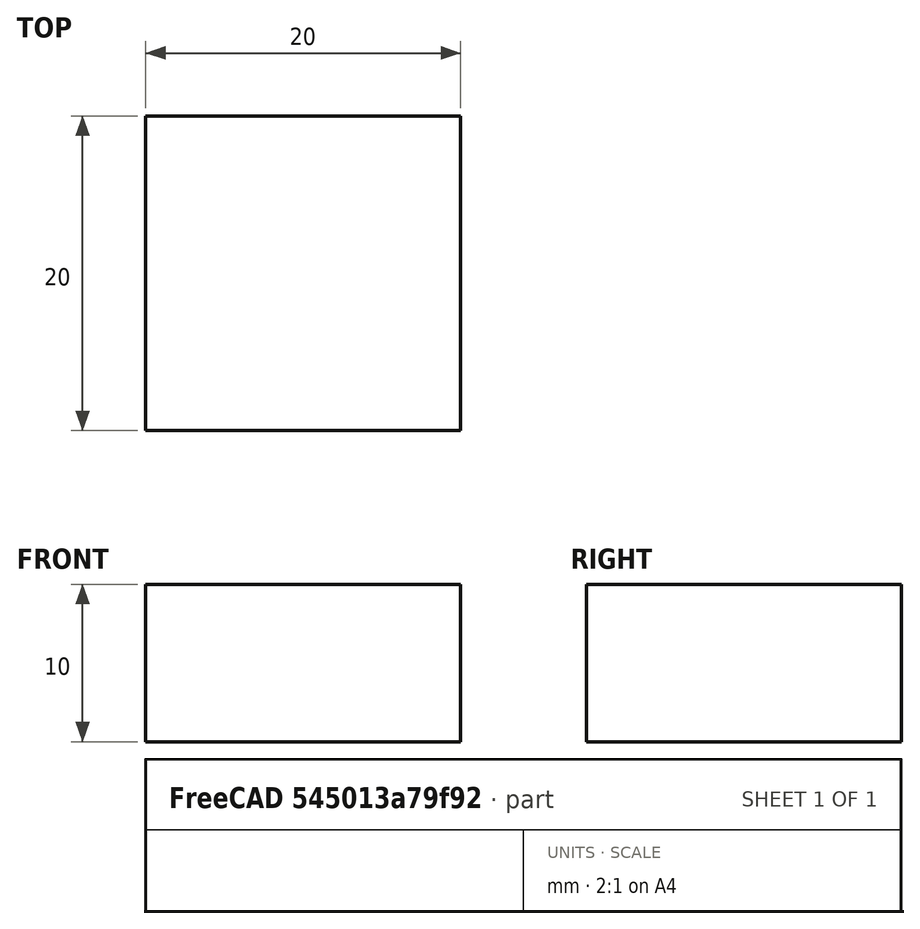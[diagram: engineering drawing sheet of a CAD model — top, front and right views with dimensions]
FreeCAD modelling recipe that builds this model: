
FCSTD DOCUMENT  (FreeCAD 0.20R29410 (Git))
Label: Spreadsheet_PartDesign_Workflow
License: All rights reserved
LicenseURL: http://en.wikipedia.org/wiki/All_rights_reserved
objects: Sketcher::SketchObject×1, Spreadsheet::Sheet×1, PartDesign::Pad×1, PartDesign::Body×1
note: 4 computed .brp shape members not serialized (recipe doc carries the construction recipe); baked Part::Feature solids carry a one-line shape summary decoded from their .brp

FEATURE [Sketcher::SketchObject] Sketch
  FullyConstrained = true
  MapMode = 5
  Support = -> [XY_Plane]
  expr: Constraints[10] = Spreadsheet.Width
  expr: Constraints[11] = Spreadsheet.Length
  sketch-geometry (5):
    g0: LineSegment StartX=-10 StartY=10 StartZ=0 EndX=-10 EndY=-10 EndZ=0
    g1: LineSegment StartX=-10 StartY=-10 StartZ=0 EndX=10 EndY=-10 EndZ=0
    g2: LineSegment StartX=10 StartY=-10 StartZ=0 EndX=10 EndY=10 EndZ=0
    g3: LineSegment StartX=10 StartY=10 StartZ=0 EndX=-10 EndY=10 EndZ=0
    g4: GeomPoint X=0 Y=0 Z=0
  constraints (12):
    c: Coincident(g0,g1)
    c: Coincident(g1,g2)
    c: Coincident(g2,g3)
    c: Coincident(g3,g0)
    c: Horizontal(g1)
    c: Horizontal(g3)
    c: Vertical(g0)
    c: Vertical(g2)
    c: Symmetric(g1,g0,g4)
    c: Coincident(g4,g-1)
    c: DistanceX(g3,g3) = 20
    c: DistanceY(g2,g2) = 20
FEATURE [Spreadsheet::Sheet] Spreadsheet
  Configuration = 1
  cells = B1=Height; C1=Width; D1=Length; A2==hiddenref(Body.Configuration.String); B2(Height)==.B6; C2(Width)==.C6; D2(Length)==.D6; A3=1x1x1; B3=10; C3=10; D3=10; A4=1x2x1; B4=10; C4=20; D4=10; A5=1x1x2; B5=10; C5=10; D5=20; A6=1x2x2; B6=10; C6=20; D6=20; A7=2x2x2; B7=20; C7=20; D7=20
  expr: .Configuration.Enum = cells[<<A3:|>>]
  expr: .cells.Bind.B2.ZZ2 = tuple(.cells; <<B>> + str(hiddenref(Body.Configuration) + 3); <<ZZ>> + str(hiddenref(Body.Configuration) + 3))
FEATURE [PartDesign::Pad] Pad
  Direction = (0,0,1)
  Length = 10
  Length2 = 10
  Profile = -> Sketch
  ReferenceAxis = -> Sketch [N_Axis]
  Type = 0
  expr: Length = Spreadsheet.Height
FEATURE [PartDesign::Body] Body
  Configuration = 3
  Group = -> [Sketch,Pad]
  Origin = -> Origin
  Tip = -> Pad
  expr: .Configuration.Enum = Spreadsheet.cells[<<A3:|>>]
